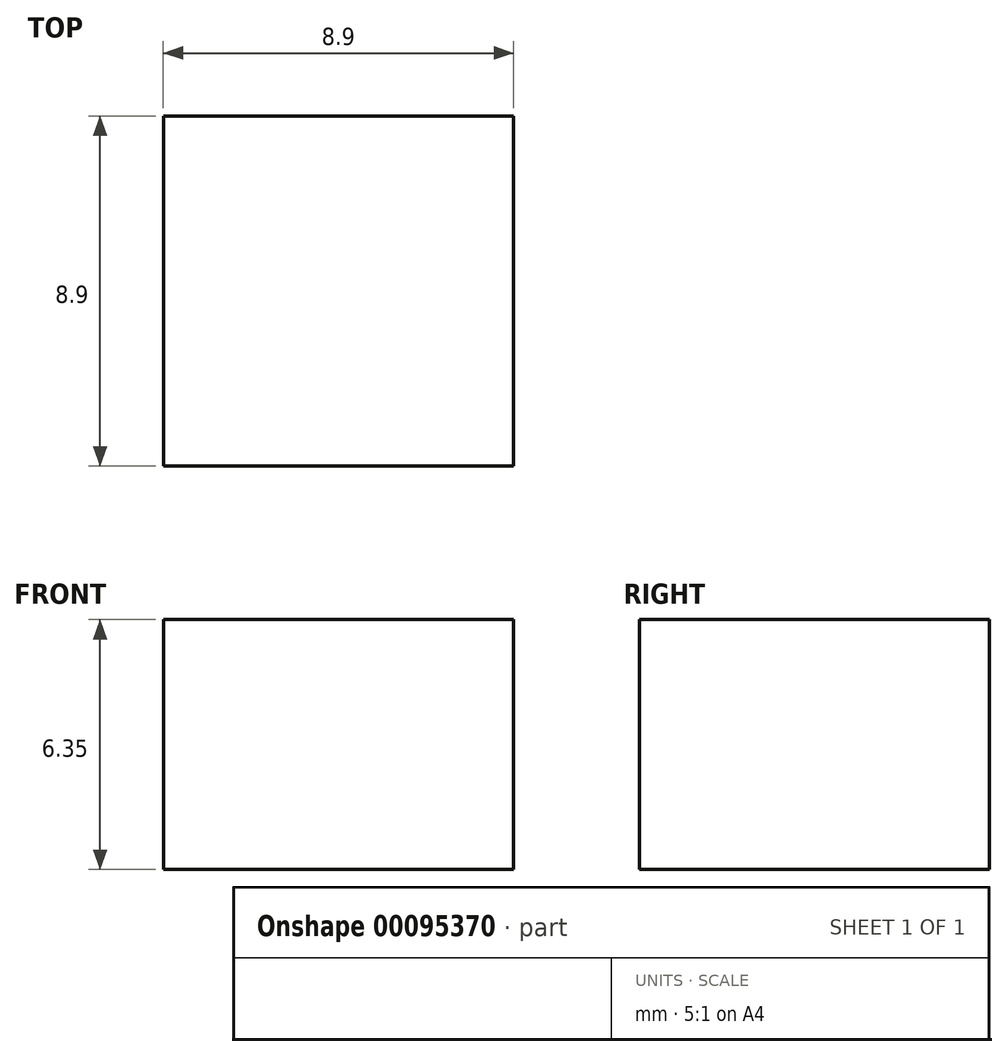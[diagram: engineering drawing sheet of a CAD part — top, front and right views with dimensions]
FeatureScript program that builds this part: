
annotation { "Feature Type Name" : "Feature", "Feature Type Description" : "" }
export const myFeature = defineFeature(function(context is Context, id is Id, definition is map)
    precondition{}
    {
        {
            var Q0;
            Q0=qCreatedBy(makeId("Top.planeOp"),FACE);
            var sketch = newSketch(context, id + "F0", { "sketchPlane" : qUnion([Q0])});
            skLineSegment(sketch, "E0.bottom", {"start": v(4.44, -4.45) * mm, "end": v(-4.45, -4.45) * mm});
            skLineSegment(sketch, "E0.top", {"start": v(4.44, 4.45) * mm, "end": v(-4.45, 4.44) * mm});
            skLineSegment(sketch, "E0.left", {"start": v(4.44, -4.45) * mm, "end": v(4.44, 4.45) * mm});
            skLineSegment(sketch, "E0.right", {"start": v(-4.45, -4.45) * mm, "end": v(-4.45, 4.44) * mm});
            skPoint(sketch, "E0.middle", {"position": v(0, 0) * mm});
            skSolve(sketch);
        }
        {
            var Q0;
            Q0 = qSketchRegion(id + "F0", true);
            extrude(context, id + "F1", {"entities" : qUnion([Q0]), "depth" : 6.35 * mm});
        }
    });
